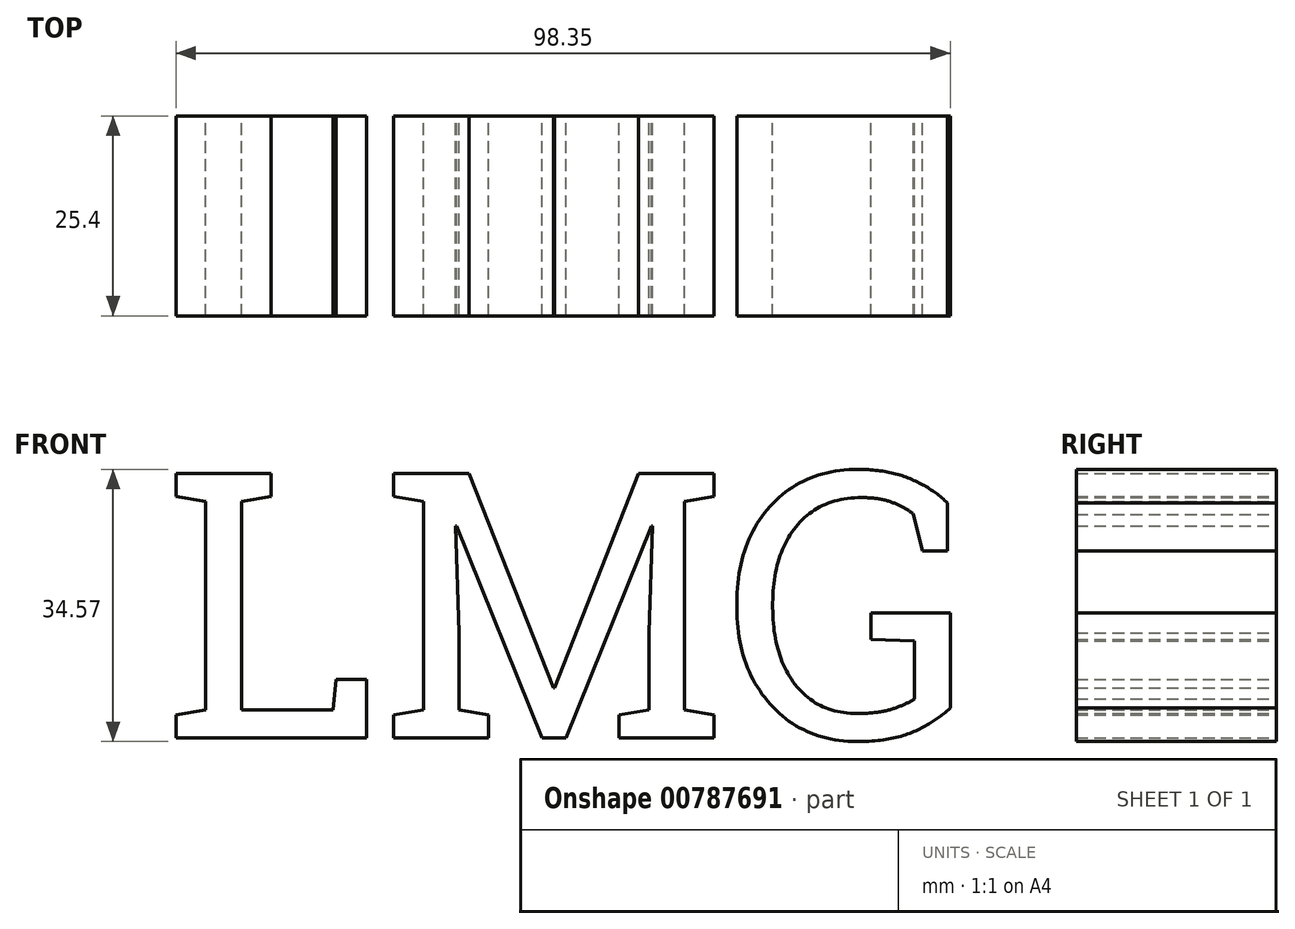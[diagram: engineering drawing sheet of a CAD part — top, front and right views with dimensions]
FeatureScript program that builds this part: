
annotation { "Feature Type Name" : "Feature", "Feature Type Description" : "" }
export const myFeature = defineFeature(function(context is Context, id is Id, definition is map)
    precondition{}
    {
        {
            var Q0;
            Q0=qCreatedBy(makeId("Front.planeOp"),FACE);
            var sketch = newSketch(context, id + "F0", { "sketchPlane" : qUnion([Q0])});
            skText(sketch, "E0", { "text": "LMG", "fontName": "RobotoSlab-Regular.ttf"});
            const initialGuessF0  = {"E0": [-0.05146, 0, 1, 0, 0.03402]};
            skSetInitialGuess(sketch, initialGuessF0);
            skSolve(sketch);
        }
        {
            var Q0;
            Q0 = qSketchRegion(id + "F0", true);
            extrude(context, id + "F1", {"entities" : qUnion([Q0]), "depth" : 25.4 * mm, "offsetDistance" : 25.4 * mm});
        }
    });
